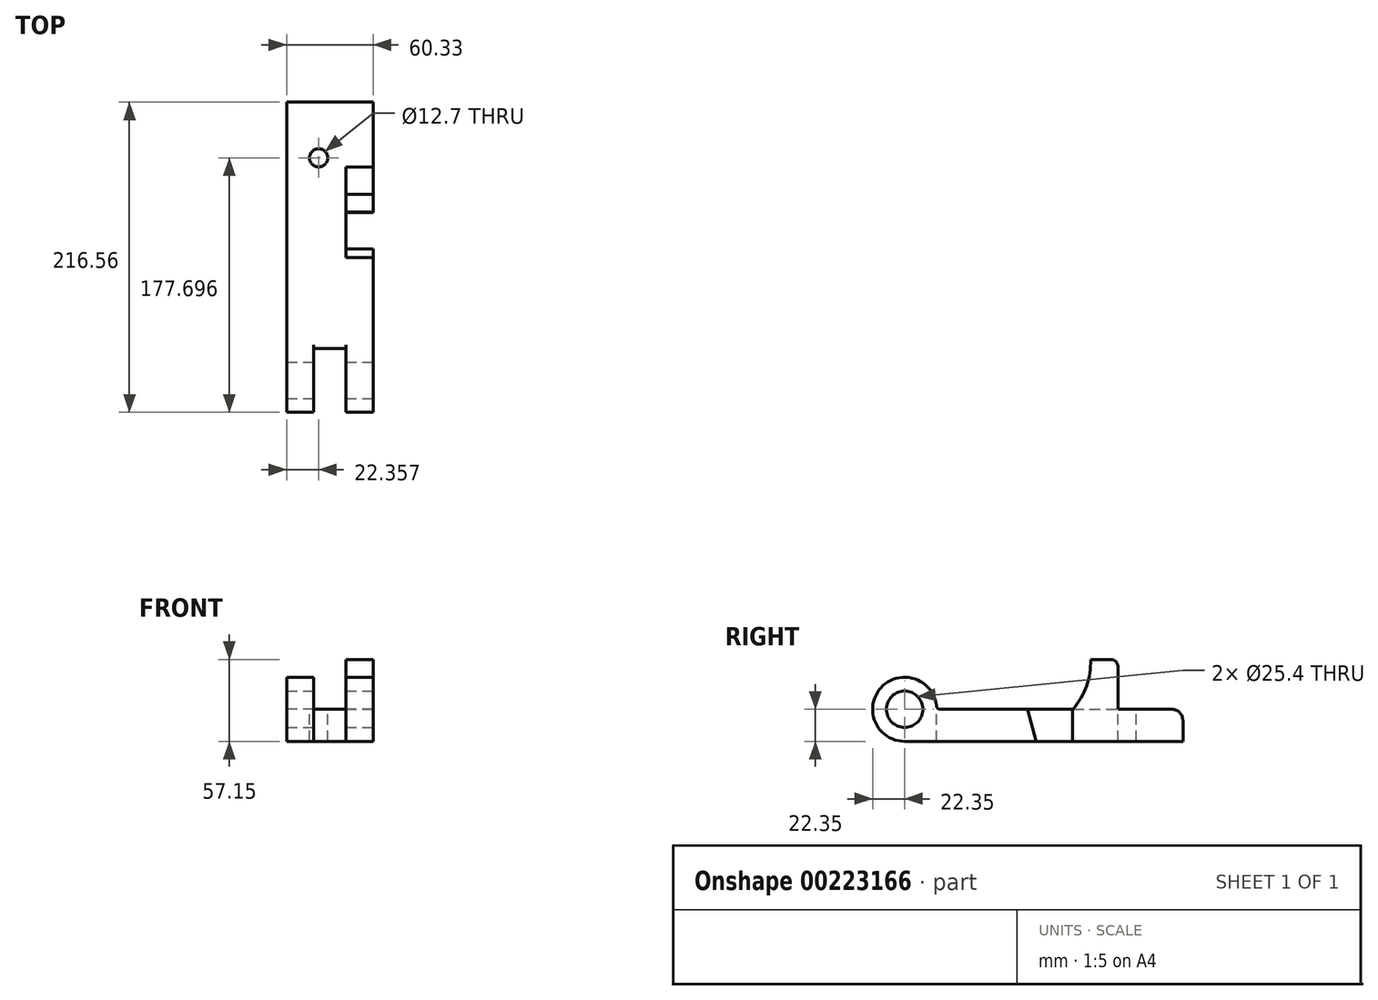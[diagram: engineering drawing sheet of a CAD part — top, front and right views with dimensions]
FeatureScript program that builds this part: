
annotation { "Feature Type Name" : "Feature", "Feature Type Description" : "" }
export const myFeature = defineFeature(function(context is Context, id is Id, definition is map)
    precondition{}
    {
        {
            var Q0;
            Q0=qCreatedBy(makeId("Right.planeOp"),FACE);
            var sketch = newSketch(context, id + "F0", { "sketchPlane" : qUnion([Q0])});
            skCircle(sketch, "E0", {"center": v(0, 0) * mm, "radius": 12.7 * mm});
            skArc(sketch, "E1", {"start": v(22.35, 0) * mm, "mid": v(-15.8, 15.8) * mm, "end": v(0, -22.35) * mm});
            skLineSegment(sketch, "E2", {"start": v(0, 0) * mm, "end": v(0, -22.35) * mm});
            skLineSegment(sketch, "E3", {"start": v(0, -22.35) * mm, "end": v(194.2, -22.35) * mm});
            skLineSegment(sketch, "E4", {"start": v(194.2, -22.35) * mm, "end": v(194.2, 0) * mm});
            skLineSegment(sketch, "E5", {"start": v(194.2, 0) * mm, "end": v(22.35, 0) * mm});
            skSolve(sketch);
        }
        {
            var Q0;
            Q0=makeQuery(id+"F0.imprint","IMPRINT",FACE,{"disambiguationData":[TD([[makeQuery(id+"F0.imprint","IMPRINT",EDGE,{"derivedFrom":sQuery(id+"F0.wireOp",EDGE,"E0")}),-1.0]])]});
            extrude(context, id + "F1", {"entities" : qUnion([Q0]), "oppositeDirection" : true, "depth" : 19 * mm});
        }
        {
            var Q0;
            Q0=qCreatedBy(makeId("Top.planeOp"),FACE);
            var sketch = newSketch(context, id + "F2", { "sketchPlane" : qUnion([Q0])});
            skLineSegment(sketch, "E6.0", {"start": v(-19, 194.2) * mm, "end": v(-19, 22.35) * mm});
            skLineSegment(sketch, "E7", {"start": v(-19, 22.35) * mm, "end": v(-41.33, 22.35) * mm});
            skLineSegment(sketch, "E8", {"start": v(-41.33, 22.35) * mm, "end": v(-41.33, 194.2) * mm});
            skLineSegment(sketch, "E9", {"start": v(-41.33, 194.2) * mm, "end": v(-19, 194.2) * mm});
            skSolve(sketch);
        }
        {
            var Q0;
            Q0 = qSketchRegion(id + "F2", true);
            extrude(context, id + "F3", {"entities" : qUnion([Q0]), "operationType" : NewBodyOperationType.ADD, "oppositeDirection" : true, "depth" : 22.35 * mm});
        }
        {
            var Q0;
            Q0=qCreatedBy(makeId("Right.planeOp"),FACE);
            cPlane(context, id + "F4", {"entities" : qUnion([Q0]), "cplaneType" : CPlaneType.OFFSET, "offset" : 41.33 * mm, "oppositeDirection" : true, "width" : 152.4 * mm, "height" : 152.4 * mm});
        }
        {
            var Q0;
            Q0=qCreatedBy(id+"F4.planeOp",FACE);
            var sketch = newSketch(context, id + "F5", { "sketchPlane" : qUnion([Q0])});
            skArc(sketch, "E10.0", {"start": v(22.35, 0) * mm, "mid": v(-15.8, 15.8) * mm, "end": v(0, -22.35) * mm});
            skLineSegment(sketch, "E11.0", {"start": v(194.2, 0) * mm, "end": v(22.35, 0) * mm});
            skLineSegment(sketch, "E12.0", {"start": v(0, -22.35) * mm, "end": v(194.2, -22.35) * mm});
            skLineSegment(sketch, "E13.0", {"start": v(194.2, -22.35) * mm, "end": v(194.2, 0) * mm});
            skCircle(sketch, "E14.0", {"center": v(0, 0) * mm, "radius": 12.7 * mm});
            skSolve(sketch);
        }
        {
            var Q0;
            Q0 = qSketchRegion(id + "F5", true);
            extrude(context, id + "F6", {"entities" : qUnion([Q0]), "operationType" : NewBodyOperationType.ADD, "oppositeDirection" : true, "depth" : 19 * mm});
        }
        {
            var Q0;
            Q0=qCreatedBy(makeId("Right.planeOp"),FACE);
            var sketch = newSketch(context, id + "F7", { "sketchPlane" : qUnion([Q0])});
            skPoint(sketch, "E15.0", {"position": v(0, 0) * mm});
            skCircle(sketch, "E16.0", {"center": v(0, 0) * mm, "radius": 12.7 * mm});
            skArc(sketch, "E17.0", {"start": v(22.35, 0) * mm, "mid": v(-15.8, 15.8) * mm, "end": v(0, -22.35) * mm});
            skLineSegment(sketch, "E18.0", {"start": v(194.2, 0) * mm, "end": v(22.35, 0) * mm});
            skLineSegment(sketch, "E19.0", {"start": v(0, -22.35) * mm, "end": v(194.2, -22.35) * mm});
            skLineSegment(sketch, "E20.0", {"start": v(194.2, -22.35) * mm, "end": v(194.2, 0) * mm});
            skLineSegment(sketch, "E21", {"start": v(0, -22.35) * mm, "end": v(91.85, -22.35) * mm});
            skLineSegment(sketch, "E22", {"start": v(0, 0) * mm, "end": v(85.85, 0) * mm});
            skLineSegment(sketch, "E23", {"start": v(0, -22.35) * mm, "end": v(117.25, -22.35) * mm});
            skLineSegment(sketch, "E24", {"start": v(117.25, -22.35) * mm, "end": v(117.25, 0) * mm});
            skLineSegment(sketch, "E25", {"start": v(117.25, 0) * mm, "end": v(85.85, 0) * mm});
            skLineSegment(sketch, "E26", {"start": v(85.85, 0) * mm, "end": v(91.85, -22.35) * mm});
            skSolve(sketch);
        }
        {
            var Q0;
            {var subQ0=sQuery(id+"F7.wireOp",EDGE,"E24");Q0=makeQuery(id+"F7.imprint","IMPRINT",FACE,{"disambiguationData":[TD([[makeQuery(id+"F7.imprint","IMPRINT",EDGE,{"derivedFrom":subQ0}),1.0]])]});}
            extrude(context, id + "F8", {"entities" : qUnion([Q0]), "operationType" : NewBodyOperationType.REMOVE, "oppositeDirection" : true, "depth" : 19.05 * mm});
        }
        {
            var Q0;
            Q0=qCreatedBy(makeId("Right.planeOp"),FACE);
            var sketch = newSketch(context, id + "F9", { "sketchPlane" : qUnion([Q0])});
            skArc(sketch, "E27.0", {"start": v(22.35, 0) * mm, "mid": v(-15.8, 15.8) * mm, "end": v(0, -22.35) * mm});
            skCircle(sketch, "E28.0", {"center": v(0, 0) * mm, "radius": 12.7 * mm});
            skLineSegment(sketch, "E29", {"start": v(0, 0) * mm, "end": v(148.82, 0) * mm});
            skLineSegment(sketch, "E30", {"start": v(148.82, 0) * mm, "end": v(148.82, 34.8) * mm});
            skLineSegment(sketch, "E31", {"start": v(148.82, 34.8) * mm, "end": v(129.77, 34.8) * mm});
            skArc(sketch, "E32", {"start": v(117.53, 0) * mm, "mid": v(126.92, 16.25) * mm, "end": v(129.77, 34.8) * mm});
            skSolve(sketch);
        }
        {
            var Q0;
            {var subQ0=sQuery(id+"F9.wireOp",EDGE,"E30");Q0=makeQuery(id+"F9.imprint","IMPRINT",FACE,{"disambiguationData":[TD([[makeQuery(id+"F9.imprint","IMPRINT",EDGE,{"derivedFrom":subQ0}),1.0]])]});}
            extrude(context, id + "F10", {"entities" : qUnion([Q0]), "operationType" : NewBodyOperationType.ADD, "oppositeDirection" : true, "depth" : 19.05 * mm});
        }
        {
            var Q0;
            Q0=makeQuery(id+"F6.boolean.opBoolean","MERGE",FACE,{"derivedFrom":[makeQuery(id+"F3.boolean.opBoolean","MERGE",FACE,{"derivedFrom":[makeQuery(id+"F1.opExtrude","SWEPT_FACE",FACE,{"disambiguationData":[OSD([sQuery(id+"F0.wireOp",EDGE,"E5")])]}),makeQuery(id+"F3.opExtrude","CAP_FACE",FACE,{"disambiguationData":[OSD([sQuery(id+"F2.wireOp",EDGE,"E6.0"),sQuery(id+"F2.wireOp",EDGE,"E7"),sQuery(id+"F2.wireOp",EDGE,"E8"),sQuery(id+"F2.wireOp",EDGE,"E9")])],"isStart":true})]}),makeQuery(id+"F6.opExtrude","SWEPT_FACE",FACE,{"disambiguationData":[OSD([sQuery(id+"F5.wireOp",EDGE,"E11.0")])]})]});
            var sketch = newSketch(context, id + "F11", { "sketchPlane" : qUnion([Q0])});
            skLineSegment(sketch, "E33.0", {"start": v(-60.33, 194.2) * mm, "end": v(-60.33, 22.35) * mm});
            skLineSegment(sketch, "E34.0", {"start": v(-60.33, 194.2) * mm, "end": v(0, 194.2) * mm});
            skCircle(sketch, "E35", {"center": v(-37.97, 155.35) * mm, "radius": 6.35 * mm});
            skSolve(sketch);
        }
        {
            var Q0;
            Q0 = qSketchRegion(id + "F11", true);
            extrude(context, id + "F12", {"entities" : qUnion([Q0]), "operationType" : NewBodyOperationType.REMOVE, "endBound" : BoundingType.THROUGH_ALL, "oppositeDirection" : true, "depth" : 25.4 * mm});
        }
        {
            var Q0;
            Q0=makeQuery(id+"F10.opExtrude","SWEPT_EDGE",EDGE,{"disambiguationData":[OSD([sQuery(id+"F9.wireOp",EDGE,"E30"),sQuery(id+"F9.wireOp",EDGE,"E31")])]});
            fillet(context, id + "F13", {"entities" : qUnion([Q0]), "radius" : 5.08 * mm, "tangentPropagation" : true, "allowEdgeOverflow" : false});
        }
        {
            var Q0;
            Q0=makeQuery(id+"F6.boolean.opBoolean","MERGE",EDGE,{"derivedFrom":[makeQuery(id+"F3.boolean.opBoolean","MERGE",EDGE,{"derivedFrom":[makeQuery(id+"F1.opExtrude","SWEPT_EDGE",EDGE,{"disambiguationData":[OSD([sQuery(id+"F0.wireOp",EDGE,"E4"),sQuery(id+"F0.wireOp",EDGE,"E5")])]}),makeQuery(id+"F3.opExtrude","CAP_EDGE",EDGE,{"disambiguationData":[OSD([sQuery(id+"F2.wireOp",EDGE,"E9")])],"isStart":true})]}),makeQuery(id+"F6.opExtrude","SWEPT_EDGE",EDGE,{"disambiguationData":[OSD([sQuery(id+"F5.wireOp",EDGE,"E11.0"),sQuery(id+"F5.wireOp",EDGE,"E13.0")])]})]});
            fillet(context, id + "F14", {"entities" : qUnion([Q0]), "radius" : 7.87 * mm, "tangentPropagation" : true, "allowEdgeOverflow" : false});
        }
        {
            var Q0;
            Q0=makeQuery(id+"F1.opExtrude","SWEPT_EDGE",EDGE,{"disambiguationData":[OSD([sQuery(id+"F0.wireOp",EDGE,"E1"),sQuery(id+"F0.wireOp",EDGE,"E5")])]});
            var Q1;
            Q1=makeQuery(id+"F6.opExtrude","SWEPT_EDGE",EDGE,{"disambiguationData":[OSD([sQuery(id+"F5.wireOp",EDGE,"E10.0"),sQuery(id+"F5.wireOp",EDGE,"E11.0")])]});
            fillet(context, id + "F15", {"entities" : qUnion([Q0, Q1]), "radius" : 2.54 * mm, "tangentPropagation" : true, "allowEdgeOverflow" : false});
        }
    });
